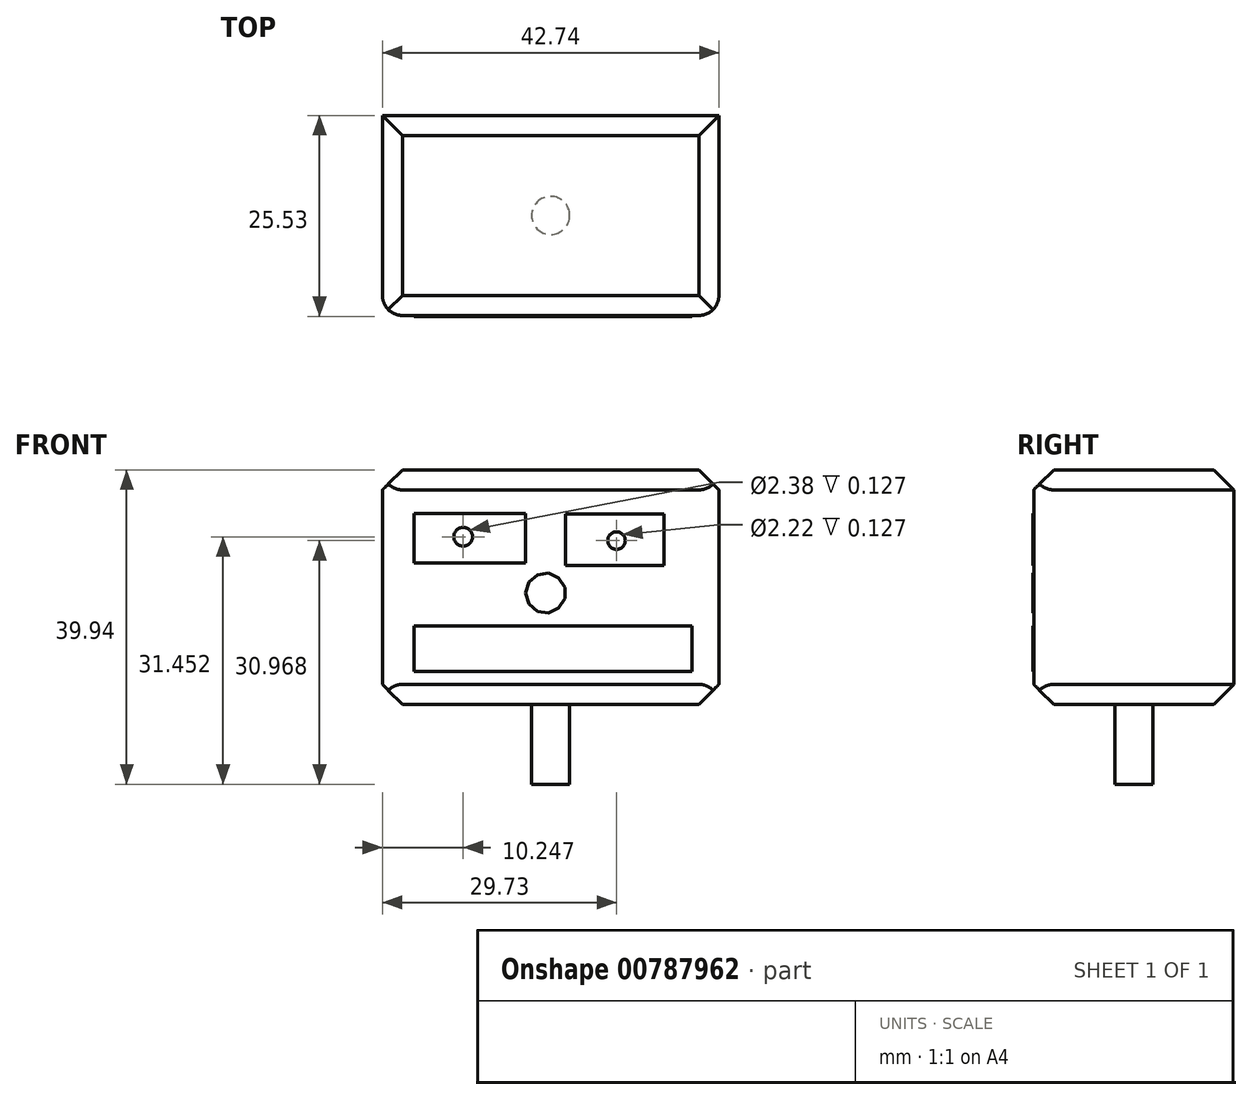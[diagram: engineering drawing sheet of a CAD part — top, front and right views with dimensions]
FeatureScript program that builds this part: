
annotation { "Feature Type Name" : "Feature", "Feature Type Description" : "" }
export const myFeature = defineFeature(function(context is Context, id is Id, definition is map)
    precondition{}
    {
        {
            var Q0;
            Q0=qCreatedBy(makeId("Front.planeOp"),FACE);
            var sketch = newSketch(context, id + "F0", { "sketchPlane" : qUnion([Q0])});
            skLineSegment(sketch, "E0.bottom", {"start": v(-36.4, 40.15) * mm, "end": v(49.07, 40.15) * mm});
            skLineSegment(sketch, "E0.top", {"start": v(-36.4, -19.43) * mm, "end": v(49.07, -19.43) * mm});
            skLineSegment(sketch, "E0.left", {"start": v(-36.4, 40.15) * mm, "end": v(-36.4, -19.43) * mm});
            skLineSegment(sketch, "E0.right", {"start": v(49.07, 40.15) * mm, "end": v(49.07, -19.43) * mm});
            skSolve(sketch);
        }
        {
            var Q0;
            Q0 = qSketchRegion(id + "F0", true);
            extrude(context, id + "F1", {"entities" : qUnion([Q0]), "depth" : 50.8 * mm, "offsetDistance" : 25.4 * mm});
        }
        {
            var Q0;
            Q0=makeQuery(id+"F1.opExtrude","CAP_FACE",FACE,{"disambiguationData":[OSD([sQuery(id+"F0.wireOp",EDGE,"E0.bottom"),sQuery(id+"F0.wireOp",EDGE,"E0.top"),sQuery(id+"F0.wireOp",EDGE,"E0.left"),sQuery(id+"F0.wireOp",EDGE,"E0.right")])],"isStart":false});
            var sketch = newSketch(context, id + "F2", { "sketchPlane" : qUnion([Q0])});
            skLineSegment(sketch, "E1.bottom", {"start": v(-28.34, 29.14) * mm, "end": v(0, 29.14) * mm});
            skLineSegment(sketch, "E1.top", {"start": v(-28.34, 16.52) * mm, "end": v(0, 16.52) * mm});
            skLineSegment(sketch, "E1.left", {"start": v(-28.34, 29.14) * mm, "end": v(-28.34, 16.52) * mm});
            skLineSegment(sketch, "E1.right", {"start": v(0, 29.14) * mm, "end": v(0, 16.52) * mm});
            skLineSegment(sketch, "E2.bottom", {"start": v(10.12, 28.93) * mm, "end": v(35.15, 28.93) * mm});
            skLineSegment(sketch, "E2.top", {"start": v(10.12, 15.84) * mm, "end": v(35.15, 15.84) * mm});
            skLineSegment(sketch, "E2.left", {"start": v(10.12, 28.93) * mm, "end": v(10.12, 15.84) * mm});
            skLineSegment(sketch, "E2.right", {"start": v(35.15, 28.93) * mm, "end": v(35.15, 15.84) * mm});
            skCircle(sketch, "E3.cCircle", {"center": v(5.06, 8.87) * mm, "radius": 4.88 * mm, "construction": true});
            skLineSegment(sketch, "E3.0", {"start": v(9.94, 10.3) * mm, "end": v(9.94, 7.44) * mm});
            skLineSegment(sketch, "E3.1", {"start": v(9.94, 7.44) * mm, "end": v(8.39, 5.02) * mm});
            skLineSegment(sketch, "E3.2", {"start": v(8.39, 5.02) * mm, "end": v(5.78, 3.83) * mm});
            skLineSegment(sketch, "E3.3", {"start": v(5.78, 3.83) * mm, "end": v(2.94, 4.24) * mm});
            skLineSegment(sketch, "E3.4", {"start": v(2.94, 4.24) * mm, "end": v(0.77, 6.12) * mm});
            skLineSegment(sketch, "E3.5", {"start": v(0.77, 6.12) * mm, "end": v(-0.03, 8.87) * mm});
            skLineSegment(sketch, "E3.6", {"start": v(-0.03, 8.87) * mm, "end": v(0.77, 11.62) * mm});
            skLineSegment(sketch, "E3.7", {"start": v(0.77, 11.62) * mm, "end": v(2.94, 13.5) * mm});
            skLineSegment(sketch, "E3.8", {"start": v(2.94, 13.5) * mm, "end": v(5.78, 13.9) * mm});
            skLineSegment(sketch, "E3.9", {"start": v(5.78, 13.9) * mm, "end": v(8.39, 12.72) * mm});
            skLineSegment(sketch, "E3.10", {"start": v(8.39, 12.72) * mm, "end": v(9.94, 10.3) * mm});
            skPoint(sketch, "E3.0.midPoint", {"position": v(9.94, 8.87) * mm});
            skLineSegment(sketch, "E4.bottom", {"start": v(-28.34, 0.54) * mm, "end": v(42.28, 0.54) * mm});
            skLineSegment(sketch, "E4.top", {"start": v(-28.34, -11.11) * mm, "end": v(42.28, -11.11) * mm});
            skLineSegment(sketch, "E4.left", {"start": v(-28.34, 0.54) * mm, "end": v(-28.34, -11.11) * mm});
            skLineSegment(sketch, "E4.right", {"start": v(42.28, 0.54) * mm, "end": v(42.28, -11.11) * mm});
            skCircle(sketch, "E5", {"center": v(-15.9, 23.16) * mm, "radius": 2.38 * mm});
            skCircle(sketch, "E6", {"center": v(23.06, 22.2) * mm, "radius": 2.22 * mm});
            skSolve(sketch);
        }
        {
            var Q0;
            Q0 = qSketchRegion(id + "F2", true);
            extrude(context, id + "F3", {"entities" : qUnion([Q0]), "operationType" : NewBodyOperationType.ADD, "depth" : 0.25 * mm, "offsetDistance" : 25.4 * mm});
        }
        {
            var Q0;
            Q0=makeQuery(id+"F1.opExtrude","SWEPT_FACE",FACE,{"disambiguationData":[OSD([sQuery(id+"F0.wireOp",EDGE,"E0.bottom")])]});
            var Q1;
            Q1=makeQuery(id+"F1.opExtrude","CAP_EDGE",EDGE,{"disambiguationData":[OSD([sQuery(id+"F0.wireOp",EDGE,"E0.bottom")])],"isStart":false});
            var Q2;
            Q2=makeQuery(id+"F1.opExtrude","SWEPT_FACE",FACE,{"disambiguationData":[OSD([sQuery(id+"F0.wireOp",EDGE,"E0.top")])]});
            chamfer(context, id + "F4", {"entities" : qUnion([Q0, Q1, Q2]), "width" : 5.08 * mm, "tangentPropagation" : true});
        }
        {
            var Q0;
            Q0=makeQuery(id+"F1.opExtrude","CAP_EDGE",EDGE,{"disambiguationData":[OSD([sQuery(id+"F0.wireOp",EDGE,"E0.left")])],"isStart":false});
            var Q1;
            Q1=makeQuery(id+"F1.opExtrude","CAP_EDGE",EDGE,{"disambiguationData":[OSD([sQuery(id+"F0.wireOp",EDGE,"E0.right")])],"isStart":false});
            fillet(context, id + "F5", {"entities" : qUnion([Q0, Q1]), "radius" : 5.08 * mm, "tangentPropagation" : true, "allowEdgeOverflow" : false});
        }
        {
            var Q0;
            Q0=makeQuery(id+"F1.opExtrude","SWEPT_BODY",BODY,{"disambiguationData":[OSD([sQuery(id+"F0.wireOp",EDGE,"E0.bottom"),sQuery(id+"F0.wireOp",EDGE,"E0.top"),sQuery(id+"F0.wireOp",EDGE,"E0.left"),sQuery(id+"F0.wireOp",EDGE,"E0.right")])]});
            var Q1;
            Q1=qCreatedBy(makeId("Origin.pointOp"),VERTEX);
            transform(context, id + "F6", {"entities" : qUnion([Q0]), "transformType" : TransformType.SCALE_UNIFORMLY, "scale" : .5, "scalePoint" : qUnion([Q1]), "makeCopy" : false});
        }
        {
            var Q0;
            Q0=makeQuery(id+"F1.opExtrude","SWEPT_FACE",FACE,{"disambiguationData":[OSD([sQuery(id+"F0.wireOp",EDGE,"E0.top")])]});
            var sketch = newSketch(context, id + "F7", { "sketchPlane" : qUnion([Q0])});
            skCircle(sketch, "E7", {"center": v(3.17, 12.7) * mm, "radius": 2.41 * mm});
            skPoint(sketch, "E7.centerSnap0", {"position": v(22, 12.7) * mm});
            skPoint(sketch, "E7.centerSnap1", {"position": v(3.17, 22.86) * mm});
            skSolve(sketch);
        }
        {
            var Q0;
            Q0=makeQuery(id+"F7.imprint","IMPRINT",FACE,{"disambiguationData":[TD([[makeQuery(id+"F7.imprint","IMPRINT",EDGE,{"derivedFrom":sQuery(id+"F7.wireOp",EDGE,"E7")}),1.0]])]});
            extrude(context, id + "F8", {"entities" : qUnion([Q0]), "operationType" : NewBodyOperationType.ADD, "depth" : 10.16 * mm, "offsetDistance" : 25.4 * mm});
        }
    });
